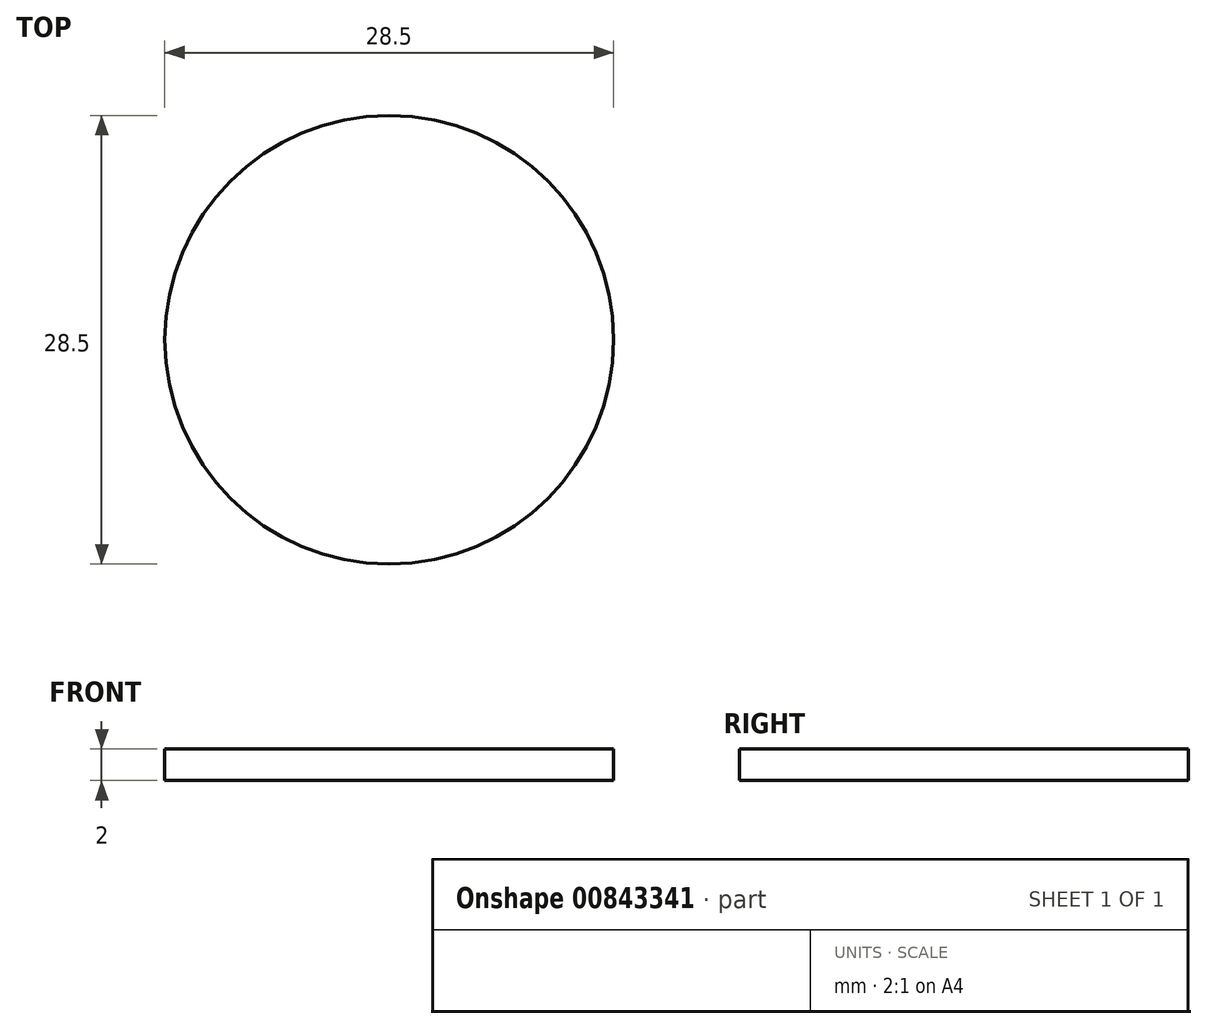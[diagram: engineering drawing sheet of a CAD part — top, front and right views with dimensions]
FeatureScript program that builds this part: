
annotation { "Feature Type Name" : "Feature", "Feature Type Description" : "" }
export const myFeature = defineFeature(function(context is Context, id is Id, definition is map)
    precondition{}
    {
        {
            var Q0;
            Q0=qCreatedBy(makeId("Top.planeOp"),FACE);
            var sketch = newSketch(context, id + "F0", { "sketchPlane" : qUnion([Q0])});
            skCircle(sketch, "E0", {"center": v(0, 0) * mm, "radius": 14.25 * mm});
            skSolve(sketch);
        }
        {
            var Q0;
            Q0 = qSketchRegion(id + "F0", true);
            extrude(context, id + "F1", {"entities" : qUnion([Q0]), "depth" : 2 * mm, "offsetDistance" : 25 * mm});
        }
    });
